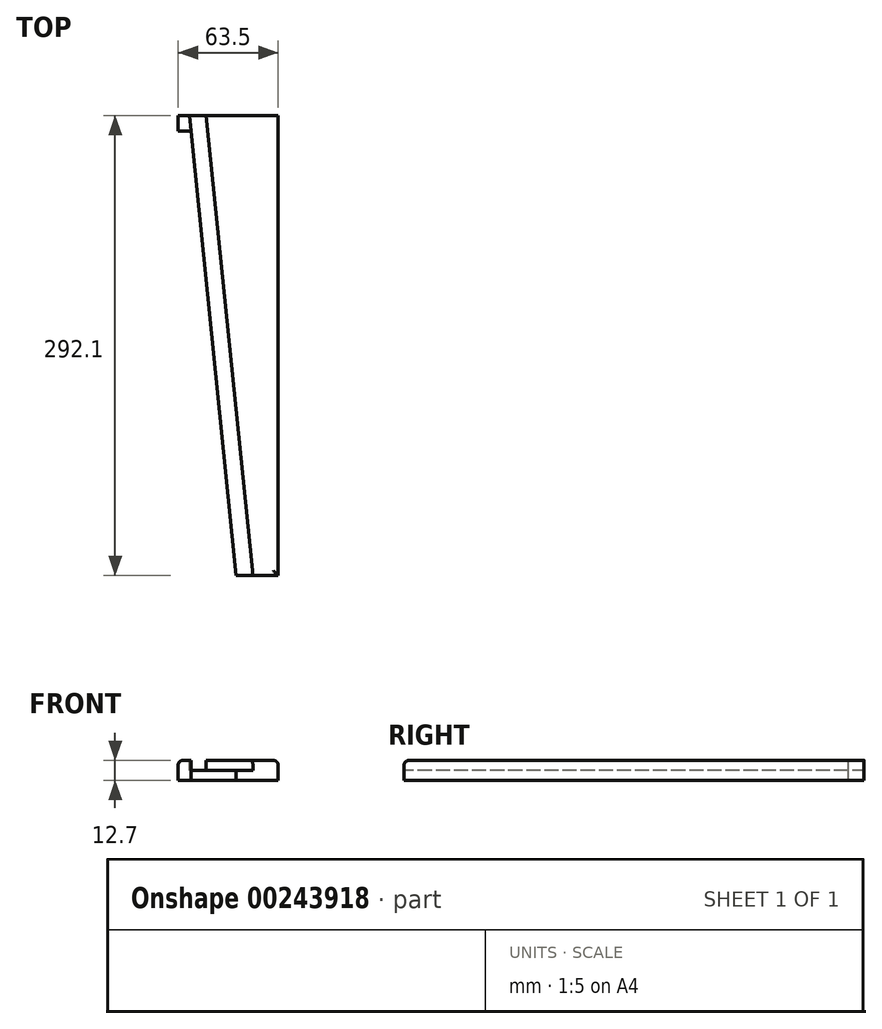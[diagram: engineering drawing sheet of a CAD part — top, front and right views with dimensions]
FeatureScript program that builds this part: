
annotation { "Feature Type Name" : "Feature", "Feature Type Description" : "" }
export const myFeature = defineFeature(function(context is Context, id is Id, definition is map)
    precondition{}
    {
        {
            var Q0;
            Q0=qCreatedBy(makeId("Top.planeOp"),FACE);
            var sketch = newSketch(context, id + "F0", { "sketchPlane" : qUnion([Q0])});
            skLineSegment(sketch, "E0.bottom", {"start": v(-74.24, 173.88) * mm, "end": v(-10.74, 173.88) * mm});
            skLineSegment(sketch, "E0.top", {"start": v(-74.24, -118.22) * mm, "end": v(-10.74, -118.22) * mm});
            skLineSegment(sketch, "E0.left", {"start": v(-74.24, 173.88) * mm, "end": v(-74.24, -118.22) * mm});
            skLineSegment(sketch, "E0.right", {"start": v(-10.74, 173.88) * mm, "end": v(-10.74, -118.22) * mm});
            skLineSegment(sketch, "E1", {"start": v(-28.4, 173.88) * mm, "end": v(-58.15, -118.22) * mm});
            skLineSegment(sketch, "E2", {"start": v(-58.15, -118.22) * mm, "end": v(-42.49, -118.22) * mm});
            skLineSegment(sketch, "E3", {"start": v(-17.9, 173.88) * mm, "end": v(-47.66, -118.22) * mm});
            skLineSegment(sketch, "E4", {"start": v(-74.24, 163.89) * mm, "end": v(-29.41, 163.89) * mm});
            skLineSegment(sketch, "E5", {"start": v(-29.41, 163.89) * mm, "end": v(-28.4, 173.88) * mm});
            skLineSegment(sketch, "E6", {"start": v(-74.24, 173.88) * mm, "end": v(-74.24, 163.89) * mm});
            skLineSegment(sketch, "E7", {"start": v(-18.92, 163.89) * mm, "end": v(-10.74, 163.89) * mm});
            skLineSegment(sketch, "E8", {"start": v(-10.74, 163.89) * mm, "end": v(-10.74, 173.88) * mm});
            skSolve(sketch);
        }
        {
            var Q0;
            {var subQ0=sQuery(id+"F0.wireOp",EDGE,"E0.left");Q0=makeQuery(id+"F0.imprint","IMPRINT",FACE,{"disambiguationData":[TD([[makeQuery(id+"F0.imprint","IMPRINT",EDGE,{"derivedFrom":subQ0}),1.0]])]});}
            var Q1;
            {var subQ0=sQuery(id+"F0.wireOp",EDGE,"E1");Q1=makeQuery(id+"F0.imprint","IMPRINT",FACE,{"disambiguationData":[TD([[makeQuery(id+"F0.imprint","IMPRINT",EDGE,{"derivedFrom":subQ0}),1.0]])]});}
            var Q2;
            {var subQ4=sQuery(id+"F0.wireOp",EDGE,"E0.right");Q2=makeQuery(id+"F0.imprint","IMPRINT",FACE,{"disambiguationData":[TD([[makeQuery(id+"F0.imprint","IMPRINT",EDGE,{"derivedFrom":subQ4}),-1.0]])]});}
            extrude(context, id + "F1", {"entities" : qUnion([Q0, Q1, Q2]), "depth" : 12.7 * mm});
        }
        {
            var Q0;
            {var subQ0=sQuery(id+"F0.wireOp",EDGE,"E1");Q0=makeQuery(id+"F0.imprint","IMPRINT",FACE,{"disambiguationData":[TD([[makeQuery(id+"F0.imprint","IMPRINT",EDGE,{"derivedFrom":subQ0}),1.0]])]});}
            extrude(context, id + "F2", {"entities" : qUnion([Q0]), "operationType" : NewBodyOperationType.REMOVE, "depth" : 6.35 * mm});
        }
        {
            var Q0;
            Q0=makeQuery(id+"F0.imprint","IMPRINT",FACE,{"disambiguationData":[TD([[makeQuery(id+"F0.imprint","IMPRINT",EDGE,{"derivedFrom":sQuery(id+"F0.wireOp",EDGE,"E4")}),1.0]])]});
            extrude(context, id + "F3", {"entities" : qUnion([Q0]), "operationType" : NewBodyOperationType.ADD, "depth" : 12.7 * mm, "hasSecondDirection" : true, "secondDirectionOppositeDirection" : false, "secondDirectionDepth" : 1.5 * mm});
        }
        {
            var Q0;
            {var subQ4=sQuery(id+"F0.wireOp",EDGE,"E7");Q0=makeQuery(id+"F0.imprint","IMPRINT",FACE,{"disambiguationData":[TD([[makeQuery(id+"F0.imprint","IMPRINT",EDGE,{"derivedFrom":subQ4}),1.0]])]});}
            extrude(context, id + "F4", {"entities" : qUnion([Q0]), "operationType" : NewBodyOperationType.ADD, "depth" : 12.7 * mm, "hasSecondDirection" : true, "secondDirectionOppositeDirection" : false, "secondDirectionDepth" : 1.5 * mm});
        }
        {
            var Q0;
            Q0=makeQuery(id+"F1.opExtrude","CAP_EDGE",EDGE,{"disambiguationData":[OSD([sQuery(id+"F0.wireOp",EDGE,"E0.left")])],"isStart":true});
            var Q1;
            Q1=makeQuery(id+"F1.opExtrude","CAP_EDGE",EDGE,{"disambiguationData":[OSD([sQuery(id+"F0.wireOp",EDGE,"E0.right")])],"isStart":true});
            var Q2;
            {var subQ1=sQuery(id+"F0.wireOp",EDGE,"E2");var subQ2=sQuery(id+"F0.wireOp",EDGE,"E0.right");var subQ3=sQuery(id+"F0.wireOp",EDGE,"E0.top");Q2=makeQuery(id+"F2.boolean.opBoolean","SPLIT",EDGE,{"disambiguationData":[TD([makeQuery(id+"F1.opExtrude","SWEPT_FACE",FACE,{"disambiguationData":[OSD([subQ2])]})])],"derivedFrom":makeQuery(id+"F1.opExtrude","CAP_EDGE",EDGE,{"disambiguationData":[OSD([subQ3,subQ1])],"isStart":true})});}
            var Q3;
            {var subQ1=sQuery(id+"F0.wireOp",EDGE,"E2");var subQ2=sQuery(id+"F0.wireOp",EDGE,"E0.left");var subQ3=sQuery(id+"F0.wireOp",EDGE,"E0.top");Q3=makeQuery(id+"F2.boolean.opBoolean","SPLIT",EDGE,{"disambiguationData":[TD([makeQuery(id+"F1.opExtrude","SWEPT_FACE",FACE,{"disambiguationData":[OSD([subQ2])]})])],"derivedFrom":makeQuery(id+"F1.opExtrude","CAP_EDGE",EDGE,{"disambiguationData":[OSD([subQ3,subQ1])],"isStart":true})});}
            fillet(context, id + "F5", {"entities" : qUnion([Q0, Q1, Q2, Q3]), "radius" : 3 * mm, "tangentPropagation" : true, "allowEdgeOverflow" : false});
        }
        {
            var Q0;
            Q0=makeQuery(id+"F1.opExtrude","SWEPT_BODY",BODY,{"disambiguationData":[OSD([sQuery(id+"F0.wireOp",EDGE,"E0.bottom"),sQuery(id+"F0.wireOp",EDGE,"E0.top"),sQuery(id+"F0.wireOp",EDGE,"E0.left"),sQuery(id+"F0.wireOp",EDGE,"E0.right"),sQuery(id+"F0.wireOp",EDGE,"E2"),sQuery(id+"F0.wireOp",EDGE,"E3"),sQuery(id+"F0.wireOp",EDGE,"E4"),sQuery(id+"F0.wireOp",EDGE,"E5"),sQuery(id+"F0.wireOp",EDGE,"E7")])]});
            var Q1;
            {var subQ0=sQuery(id+"F0.wireOp",EDGE,"E2");var subQ1=sQuery(id+"F0.wireOp",EDGE,"E0.top");var subQ2=sQuery(id+"F0.wireOp",EDGE,"E7");var subQ3=sQuery(id+"F0.wireOp",EDGE,"E0.right");var subQ4=sQuery(id+"F0.wireOp",EDGE,"E3");Q1=makeQuery(id+"F5.opFillet","BLEND_EDGE",EDGE,{"blendedFrom":[makeQuery(id+"F1.opExtrude","CAP_EDGE",EDGE,{"disambiguationData":[OSD([subQ3])],"isStart":true}),makeQuery(id+"F2.boolean.opBoolean","SPLIT",FACE,{"disambiguationData":[TD([makeQuery(id+"F1.opExtrude","SWEPT_FACE",FACE,{"disambiguationData":[OSD([subQ3])]})])],"derivedFrom":makeQuery(id+"F1.opExtrude","CAP_FACE",FACE,{"disambiguationData":[OSD([sQuery(id+"F0.wireOp",EDGE,"E0.bottom"),subQ1,sQuery(id+"F0.wireOp",EDGE,"E0.left"),subQ3,subQ0,subQ4,sQuery(id+"F0.wireOp",EDGE,"E4"),sQuery(id+"F0.wireOp",EDGE,"E5"),subQ2])],"isStart":true})})],"blendedInto":[makeQuery(id+"F2.boolean.opBoolean","SPLIT",FACE,{"disambiguationData":[TD([makeQuery(id+"F1.opExtrude","SWEPT_FACE",FACE,{"disambiguationData":[OSD([subQ3])]})])],"derivedFrom":makeQuery(id+"F1.opExtrude","CAP_FACE",FACE,{"disambiguationData":[OSD([sQuery(id+"F0.wireOp",EDGE,"E0.bottom"),subQ1,sQuery(id+"F0.wireOp",EDGE,"E0.left"),subQ3,subQ0,subQ4,sQuery(id+"F0.wireOp",EDGE,"E4"),sQuery(id+"F0.wireOp",EDGE,"E5"),subQ2])],"isStart":true})})]});}
            transform(context, id + "F6", {"entities" : qUnion([Q0]), "transformType" : TransformType.ROTATION, "transformAxis" : qUnion([Q1]), "angle" : 180 * degree, "makeCopy" : false});
        }
    });
